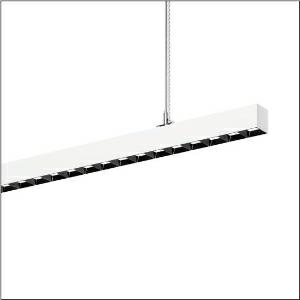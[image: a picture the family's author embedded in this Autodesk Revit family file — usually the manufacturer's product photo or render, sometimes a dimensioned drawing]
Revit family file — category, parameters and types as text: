
# Revit family: silica_r__21_51mx31dc4dwb_7dad
name_source: partatom
category: Lighting Fixtures
units: mm (PartAtom-declared; Revit-internal decimal feet)

## family parameters
Cut with Voids When Loaded = No
Host = Face
Light Source = No
Part Type = Normal
Room Calculation Point = No
Round Connector Dimension = Use Diameter
Shared = No

## types (1)
- --- (1 x LED, 18230 lm, 105.9 W, 4000K)
    Apparent Load = 106 VA
    CIE Flux Codes = 87 99 100 59 100
    Color Rendering = 80
    Color Temperature = 4000K
    Default Elevation = 1800 mm
    Description = Silica® 21, office luminaire, primary light control with darklight reflector, of PMMA, black, CAT 2 (L<= 3000cd/m²), light emission: direct/indirect distribution, primary light characteristic: symmetric, installation type: suspended mounting, LED, rated luminous flux: 18.230lm, luminous efficacy: 172lm/W, light colour: 840, colour temperature: 4000K, with terminal, 3+2-pole, max. 2.5mm², mains connection: 220..240V, AC, 50/60Hz, rated input power: 105.9W, luminaire housing, of aluminium, traffic white (RAL 9016), length: 3.004mm, width: 53mm, height: 53mm, protection rating (complete): IP20, insulation class (complete): insulation class I (protective earthing), certification: CE, permissible operating ambient temperature: 0..+35°C, standard: EN 50419, packaging unit: 1 piece
    Height = 53 mm
    Lamp = 1 x LED
    Lamp Light Flux = 18230 lm
    Lamp Power = 105.9 W
    Lamp count = 1
    Length = 3004 mm
    Luminous efficacy = 172 lm/W
    Manufacturer = Siteco
    ModVariant = No
    Model = 51MX31DC4DWB
    Mounting Place = Ceiling
    Mounting Type = Pendant
    Number of Poles = 1
    OnlyDefault = Yes
    Power Factor = 1
    Product Name = Silica® 21
    Product group = office luminaire | ceiling pendant
    ProductGroupID = 905
    Protection Class = Protection class I
    Protection Degree = IP 20
    RLX_Detail_Level = 1
    RlxData = <blob elided: 64685 chars, md5=b9b5d45f>
    Socket = socket
    Standby Power = 0 W
    System Light Flux = 18230 lm
    System Power = 106 W
    Type Comments = factory setting: luminous flux: 100 % | dim-lin: 254 | 367 mA
    Type Image = l_1251637.jpg
    URL = http://relux.com
    VarID = @adj_030287
    Voltage = 0 V
    Weight = 0.00 kg
    Width = 53 mm

## geometry (parser evidence)
native form markers: Blend x4, Sweep x12
no freeform markers — native parametric forms only
